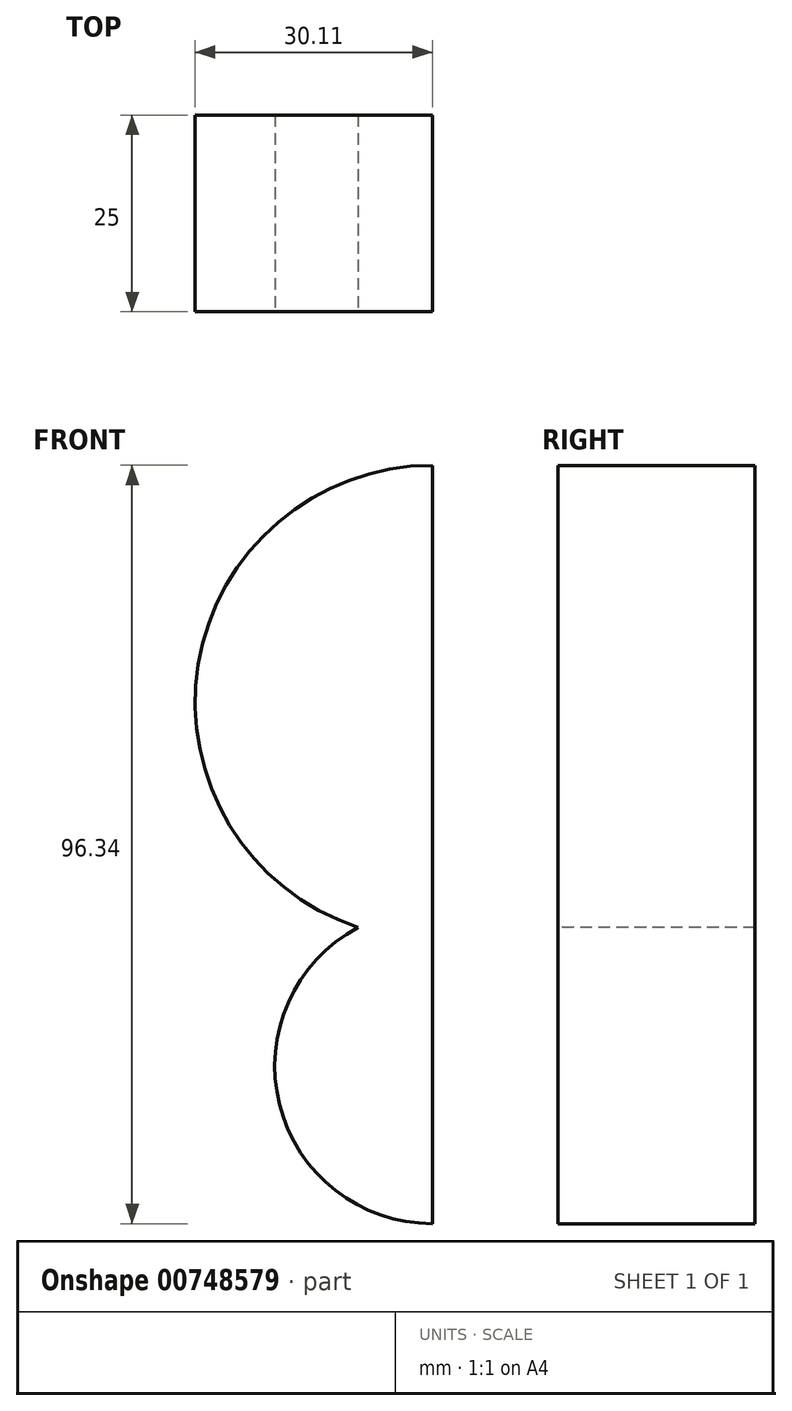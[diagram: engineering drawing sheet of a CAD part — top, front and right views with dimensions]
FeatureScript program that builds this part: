
annotation { "Feature Type Name" : "Feature", "Feature Type Description" : "" }
export const myFeature = defineFeature(function(context is Context, id is Id, definition is map)
    precondition{}
    {
        {
            var Q0;
            Q0=qCreatedBy(makeId("Front.planeOp"),FACE);
            var sketch = newSketch(context, id + "F0", { "sketchPlane" : qUnion([Q0])});
            skArc(sketch, "E0", {"start": v(-9.43, 17.64) * mm, "mid": v(-19.4, -4.86) * mm, "end": v(0, -20) * mm});
            skArc(sketch, "E1", {"start": v(0, 76.34) * mm, "mid": v(-29.73, 51) * mm, "end": v(-9.43, 17.64) * mm});
            skLineSegment(sketch, "E2", {"start": v(0, -20) * mm, "end": v(0, 76.34) * mm});
            skSolve(sketch);
        }
        {
            var Q0;
            Q0=makeQuery(id+"F0.imprint","IMPRINT",FACE,{"disambiguationData":[TD([[makeQuery(id+"F0.imprint","IMPRINT",EDGE,{"derivedFrom":sQuery(id+"F0.wireOp",EDGE,"E0")}),1.0]])]});
            extrude(context, id + "F1", {"entities" : qUnion([Q0]), "endBound" : BoundingType.SYMMETRIC, "oppositeDirection" : true, "depth" : 25 * mm, "offsetDistance" : 25 * mm});
        }
    });
